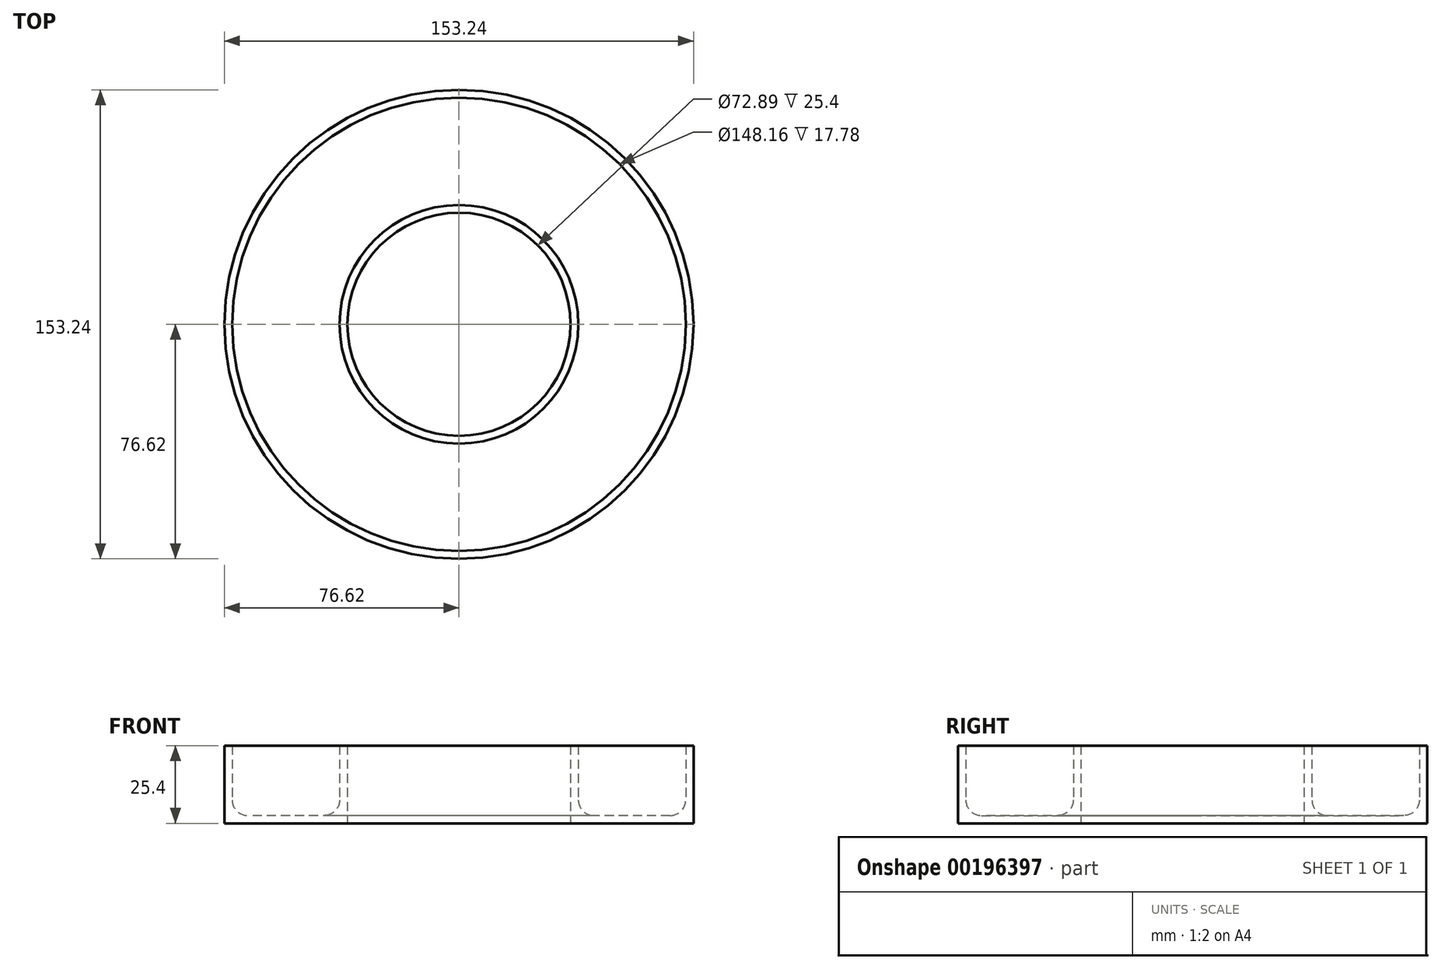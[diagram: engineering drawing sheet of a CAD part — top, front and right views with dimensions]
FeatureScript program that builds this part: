
annotation { "Feature Type Name" : "Feature", "Feature Type Description" : "" }
export const myFeature = defineFeature(function(context is Context, id is Id, definition is map)
    precondition{}
    {
        {
            var Q0;
            Q0=qCreatedBy(makeId("Top.planeOp"),FACE);
            var sketch = newSketch(context, id + "F0", { "sketchPlane" : qUnion([Q0])});
            skCircle(sketch, "E0", {"center": v(0, 0) * mm, "radius": 76.62 * mm});
            skCircle(sketch, "E1", {"center": v(0, 0) * mm, "radius": 36.45 * mm});
            skSolve(sketch);
        }
        {
            var Q0;
            Q0 = qSketchRegion(id + "F0", true);
            extrude(context, id + "F1", {"entities" : qUnion([Q0]), "depth" : 25.4 * mm});
        }
        {
            var Q0;
            Q0=makeQuery(id+"F1.opExtrude","CAP_FACE",FACE,{"disambiguationData":[OSD([sQuery(id+"F0.wireOp",EDGE,"E0"),sQuery(id+"F0.wireOp",EDGE,"E1")])],"isStart":false});
            shell(context, id + "F2", {"entities" : qUnion([Q0]), "thickness" : 2.54 * mm});
        }
        {
            var Q0;
            {var subQ0=sQuery(id+"F0.wireOp",EDGE,"E1");var subQ1=sQuery(id+"F0.wireOp",EDGE,"E0");Q0=makeQuery(id+"F2.opShell","OFFSET_FACE",FACE,{"disambiguationData":[OSD([subQ1,subQ0]),TDD([makeQuery(id+"F1.opExtrude","CAP_FACE",FACE,{"disambiguationData":[OSD([subQ1,subQ0])],"isStart":true})])]});}
            fillet(context, id + "F3", {"entities" : qUnion([Q0]), "radius" : 5.08 * mm, "tangentPropagation" : true, "allowEdgeOverflow" : false});
        }
    });
